# Revit family: LCVRL
name_source: partatom
category: Lighting Fixtures
revit_build: Autodesk Revit 2014 (Build: 20130308_1515(x64)
units: mm (PartAtom-declared; Revit-internal decimal feet)

## types (2) — shared parameters
Apparent Load = 50 VA
Assembly Code = D5020200
Certifications = All luminaires are built to UL and CSA standards
Color Filter = 16777215
Connector Description = Lighting Connector
Default Elevation = 48 "
Description = Direct-Indirect distribution in an elegantly curved shape with high performance LED technology. Providing lumen packages from 3200 to 7500 and options to vary the amount of direct and indirect lighitng, Curv Radial Lens LED is an attractive solution for office, education, and health care environments.
Dimming Lamp Color Temperature Shift = <None>
Emit Shape Visible in Rendering = No
Emit from Rectangle Width = 8 "
Features = Acrylic radial lens combines with curved shape for direct/indirect, direct distribution
Lumen packages range from 3200 to 7500
Up/down switching available on some models
Long-life LED is rated L90 at 60,000 hours, with projected life over 100,000 to reduce facility maintenance
Four LED CCT color choices
Controls compatible
Available with optional installed daylight sensors
Flat end standard
Sculpted or bull nose end caps optional
Modular mounting points for convenient hanging locations
Aircraft cable mounting
Straight rows assured using die cast aluminium tongue-and-groove patented couplers.
Five year warranty
DLC® (DesignLights Consortium) Qualified, with some Premium Qualified configurations - see www.designlights.org
SpectraSync™ Color Tuning Technology available
NX Distributed Intelligence™ wired and wireless controls capability available
Housing Material = Paint - Hubbell - Matte White
Lamp = LED
Load Classification = Lighting
Manufacturer = Alera Lighting
Model = LCVRL
Photometric Note = For more ies file please find the above Photometric Web Link
Photometric Web File = LCVR-L-35LW-100.IES
Photometric Web Link = https://www.hubbell.com
Power Factor = 1
Product Doucmentation Link = https://hubbellcdn.com
Product Page URL = https://www.hubbell.com
Reflector Finish = Hubbell - White Glass
Tilt Angle = -90.00°
URL = https://www.hubbell.com
Voltage = 120 V
Warranty = 5 years Warranty
Watts = 50 W
Width = 11.63 "
Width 1 = 5 "

## per-type parameters (varying)
| type | Emit from Rectangle Length | Length |
| LCVRL-4' | 47 " | 48 " |
| LCVRL-8' | 95 " | 96 " |

## geometry (parser evidence)
native form markers: Blend x17, Sweep x3
no freeform markers — native parametric forms only
